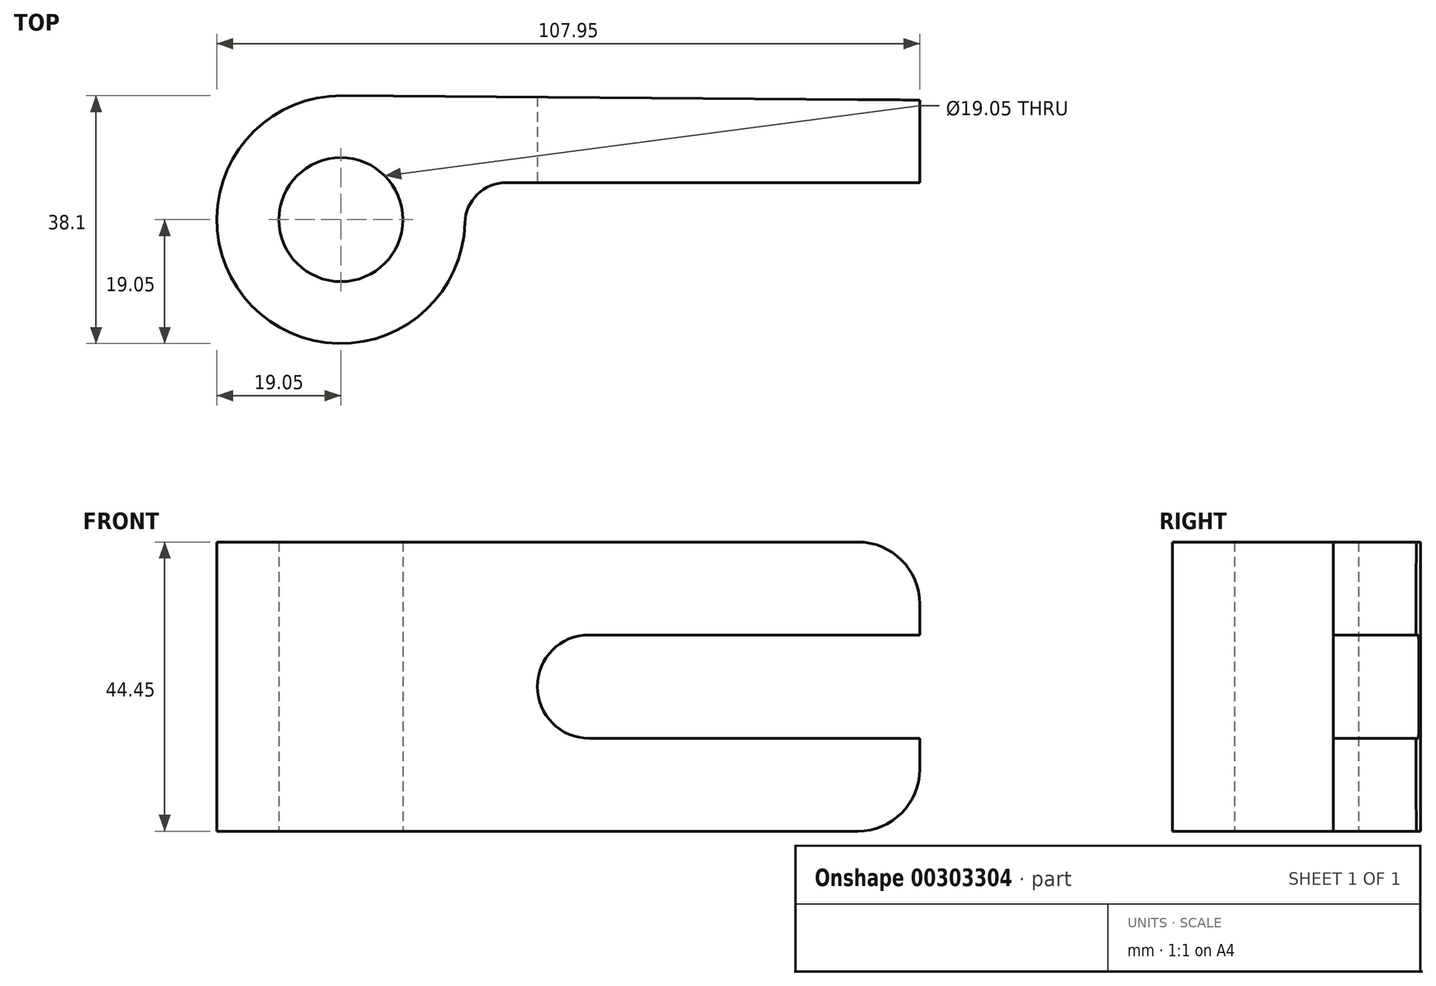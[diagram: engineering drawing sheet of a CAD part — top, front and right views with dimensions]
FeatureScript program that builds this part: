
annotation { "Feature Type Name" : "Feature", "Feature Type Description" : "" }
export const myFeature = defineFeature(function(context is Context, id is Id, definition is map)
    precondition{}
    {
        {
            var Q0;
            Q0=qCreatedBy(makeId("Top.planeOp"),FACE);
            var sketch = newSketch(context, id + "F0", { "sketchPlane" : qUnion([Q0])});
            skArc(sketch, "E0", {"start": v(0.14, 19.05) * mm, "mid": v(-13.7, -13.24) * mm, "end": v(19.04, -0.5) * mm});
            skCircle(sketch, "E1", {"center": v(0, 0) * mm, "radius": 9.53 * mm});
            skLineSegment(sketch, "E2", {"start": v(0, 19.05) * mm, "end": v(88.9, 18.38) * mm});
            skLineSegment(sketch, "E3", {"start": v(88.9, 18.38) * mm, "end": v(88.9, 5.68) * mm});
            skLineSegment(sketch, "E4", {"start": v(88.9, 5.68) * mm, "end": v(25.4, 5.68) * mm});
            skArc(sketch, "E5", {"start": v(25.4, 5.68) * mm, "mid": v(20.96, 3.88) * mm, "end": v(19.04, -0.5) * mm});
            skSolve(sketch);
        }
        {
            var Q0;
            Q0 = qSketchRegion(id + "F0", true);
            extrude(context, id + "F1", {"entities" : qUnion([Q0]), "depth" : 44.45 * mm, "offsetDistance" : 25.4 * mm});
        }
        {
            var Q0;
            Q0=makeQuery(id+"F1.opExtrude","SWEPT_FACE",FACE,{"disambiguationData":[OSD([sQuery(id+"F0.wireOp",EDGE,"E4")])]});
            var sketch = newSketch(context, id + "F2", { "sketchPlane" : qUnion([Q0])});
            skLineSegment(sketch, "E6", {"start": v(88.9, 22.23) * mm, "end": v(38.1, 22.23) * mm, "construction": true});
            skArc(sketch, "E7", {"start": v(38.1, 30.16) * mm, "mid": v(30.16, 22.23) * mm, "end": v(38.1, 14.29) * mm});
            skLineSegment(sketch, "E8", {"start": v(38.1, 30.16) * mm, "end": v(88.9, 30.16) * mm});
            skLineSegment(sketch, "E9.MirrorCS", {"start": v(38.1, 14.29) * mm, "end": v(88.9, 14.29) * mm});
            skLineSegment(sketch, "E10", {"start": v(88.9, 44.45) * mm, "end": v(79.37, 44.45) * mm});
            skLineSegment(sketch, "E11", {"start": v(79.37, 44.45) * mm, "end": v(79.37, 34.93) * mm});
            skArc(sketch, "E12", {"start": v(88.9, 34.93) * mm, "mid": v(86.1, 41.66) * mm, "end": v(79.37, 44.45) * mm});
            skLineSegment(sketch, "E13", {"start": v(88.9, 44.45) * mm, "end": v(88.9, 30.16) * mm});
            skLineSegment(sketch, "E14.MirrorCS", {"start": v(88.9, 0) * mm, "end": v(88.9, 14.29) * mm});
            skLineSegment(sketch, "E15.MirrorCS", {"start": v(88.9, 0) * mm, "end": v(79.37, 0) * mm});
            skArc(sketch, "E16.MirrorCS", {"start": v(88.9, 9.52) * mm, "mid": v(86.1, 2.79) * mm, "end": v(79.37, 0) * mm});
            skSolve(sketch);
        }
        {
            var Q0;
            Q0 = qSketchRegion(id + "F2", true);
            var Q1;
            Q1=makeQuery(id+"F2.imprint","IMPRINT",FACE,{"disambiguationData":[TD([[makeQuery(id+"F2.imprint","IMPRINT",EDGE,{"derivedFrom":sQuery(id+"F2.wireOp",EDGE,"E7")}),1.0]])]});
            extrude(context, id + "F3", {"entities" : qUnion([Q0, Q1]), "operationType" : NewBodyOperationType.REMOVE, "endBound" : BoundingType.UP_TO_NEXT, "oppositeDirection" : true, "depth" : 25.4 * mm, "offsetDistance" : 25.4 * mm});
        }
    });
